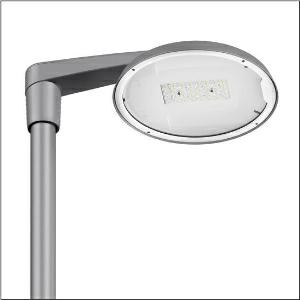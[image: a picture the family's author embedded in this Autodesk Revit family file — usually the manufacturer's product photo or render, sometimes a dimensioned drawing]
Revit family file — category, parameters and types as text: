
# Revit family: dl_r__50_iq_mini___st0_5a_5xa248b41f08fe_8feb
name_source: partatom
category: Lighting Fixtures
units: mm (PartAtom-declared; Revit-internal decimal feet)

## family parameters
Cut with Voids When Loaded = No
Host = Face
Light Source = No
Part Type = Normal
Room Calculation Point = No
Round Connector Dimension = Use Diameter
Shared = No

## types (1)
- --- (1 x LED, 2690 lm, 15.7 W, 4000K)
    Apparent Load = 16 VA
    CIE Flux Codes = 41 75 97 100 100
    Color Rendering = 70
    Color Temperature = 4000K
    Default Elevation = 1800 mm
    Description = DL® 50 iQ mini, mast luminaire, primary light control with lens, of PMMA, primary optical cover: cover, of toughened safety glass, transparent, light distribution: ST0.5a, light emission: direct distribution, primary light characteristic: asymmetric, installation type: side-entry, post-top, LED, High Power LED, rated luminous flux: 2.690lm, luminous efficacy: 171lm/W, light colour: 740, colour temperature: 4000K, control: optimised constant luminous flux control (CLO 2.0), Desk-Remote (wireless, voltage-free reading and setting of iQ features in the workshop via application-optimized NFC function/RFID function), Light-Fading, Smart-Wire, Night-Set, Lumen-Switch, Temp-Guard, Auto-Match, Street-Remote, mains connection: 230..240V, AC, 50/60Hz, connection cable pre-assembled, cable length: 6,5m, start of lifetime: 16W, end of service life: 16W, reduction: 8W, luminaire housing, of diecast aluminium, powder-coated, Siteco® metallic grey (DB 702S), inclination adjustable: 0°, 5°, 10° (post-top) | 0°, -5°, -10°, -15° (side-entry), please order mast post-top element or mast side-entry element separately, diameter: 500mm, height: 115mm, post-top: for spigot size d x l = 76 x 100mm; with reducer (optional accessory) 60 x 100mm | side-entry: for spigot size d x l = 60 x 100mm; with reducer (optional accessory) 42 x 100mm, protection rating (complete): IP66, insulation class (complete): insulation class II (safety insulation), certification: CE, ENEC, VDE, impact resistance: IK08, permissible operating ambient temperature for outdoor applications: -25..+40°C, standard-compliant lighting for roads and squares, packaging unit: 1 piece

Light Distribution: ST0.5a
    Height = 115 mm
    Lamp = 1 x LED
    Lamp Light Flux = 2690 lm
    Lamp Power = 15.7 W
    Lamp count = 1
    Length = 500 mm
    Luminous efficacy = 171 lm/W
    Manufacturer = Siteco
    ModVariant = No
    Model = 5XA248B41F08FE
    Number of Poles = 1
    OnlyDefault = Yes
    Power Factor = 1
    Product Name = DL® 50 iQ mini | ST0.5a
    Product group = mast luminaire | pylon top
    ProductGroupID = 6100
    Protection Class = Protection class II
    Protection Degree = IP 66
    RLX_Detail_Level = 1
    RLX_Emergency_Light_Flux = 0 lm
    RLX_Emergency_Type = 0
    RLX_Emergency_Type_DB = No
    RlxData = <blob elided: 126381 chars, md5=1c28885c>
    Socket = socket
    Standby Power = 0 W
    System Light Flux = 2690 lm
    System Power = 16 W
    Type Comments = factory setting: luminous flux: 100 % | dim-lin: 254 | 319 mA
    Type Image = l_1251794.jpg
    URL = http://relux.com
    VarID = @adj_088765
    Voltage = 0 V
    Weight = 0.00 kg
    Width = 0 mm  [stored 0 ft]

note: [stored X ft] marks values corroborated as IEEE doubles in the binary element streams (Revit-internal decimal feet)

## geometry (parser evidence)
native form markers: Blend x4, Sweep x11
no freeform markers — native parametric forms only
